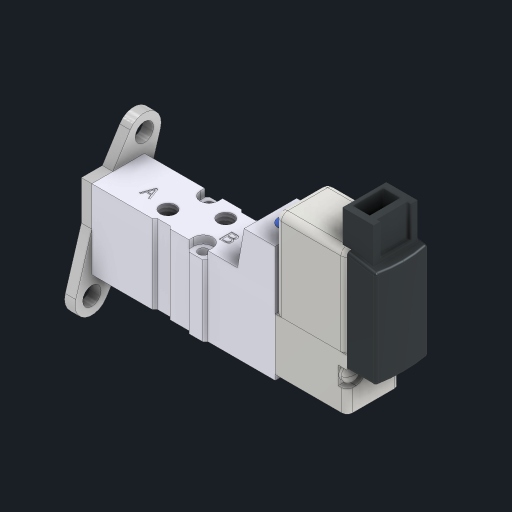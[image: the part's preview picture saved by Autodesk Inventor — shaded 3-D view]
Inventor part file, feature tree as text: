
AUTODESK INVENTOR PART (.ipt)
format: ipt  version: 2023 (Build 270158030, 158C)  size: 553,472 bytes
history: native  units: in
note: dims shown in document units (in); Inventor stores cm internally (conversion verified against a paired STEP export)
features: other x7, thread x5
ambient origin geometry x8: Origin, YZ Plane, XZ Plane, XY Plane, X Axis, Y Axis, Z Axis, Center Point
bodies: Solid1 (feature_tree)
feature tree (12):
  other  "Solenoid, Fwd, Reverse.iam"
  other  "Valve Body.ipt:1"
  other  "SYJ3120-SMO-M3-F.step_V100_V111-SMO.iam:1::SYJ3120-SMO-M3-F.step_V100_1.ipt:1"
  other  "SYJ3120-SMO-M3-F.step_V100_V111-SMO.iam:1::Cover.ipt:1"
  other  "Bracket.ipt:1"
  other  "SY113-SMO-PM3-F.step_MAN-OPA_P.ipt:1"
  other  "Solenoid, Fwd, Reverse.iam_Bodies"
  thread  "Thread1"  [1 undecoded]
  thread  "Thread2"  [1 undecoded]
  thread  "Thread3"  [1 undecoded]
  thread  "Thread4"  [1 undecoded]
  thread  "Thread5"  [1 undecoded]
note: 5 required parameter values undecoded (feature->parameter linkage not recoverable at this tier; creation-order binding heuristic only, values carry confidence <= 0.55)
